annotation { "Feature Type Name" : "Feature", "Feature Type Description" : "" }
export const myFeature = defineFeature(function(context is Context, id is Id, definition is map)
    precondition{}
    {
        {
            var Q0;
            Q0=qCreatedBy(makeId("Front.planeOp"),FACE);
            var sketch = newSketch(context, id + "F0", { "sketchPlane" : qUnion([Q0])});
            skLineSegment(sketch, "E0.bottom", {"start": v(-36.81, 42.63) * mm, "end": v(35.22, 42.63) * mm});
            skLineSegment(sketch, "E0.top", {"start": v(-36.81, -38.86) * mm, "end": v(35.22, -38.86) * mm});
            skLineSegment(sketch, "E0.left", {"start": v(-36.81, 42.63) * mm, "end": v(-36.81, -38.86) * mm});
            skLineSegment(sketch, "E0.right", {"start": v(35.22, 42.63) * mm, "end": v(35.22, -38.86) * mm});
            skPoint(sketch, "E1.oppositeSnap0", {"position": v(-0.8, 42.63) * mm});
            skLineSegment(sketch, "E1.bottom", {"start": v(-26.75, 18.27) * mm, "end": v(-0.8, 18.27) * mm});
            skLineSegment(sketch, "E1.top", {"start": v(-26.75, 12.97) * mm, "end": v(-0.8, 12.97) * mm});
            skLineSegment(sketch, "E1.left", {"start": v(-26.75, 18.27) * mm, "end": v(-26.75, 12.97) * mm});
            skLineSegment(sketch, "E1.right", {"start": v(-0.8, 18.27) * mm, "end": v(-0.8, 12.97) * mm});
            skLineSegment(sketch, "E2.bottom", {"start": v(-27.28, 28.86) * mm, "end": v(-0.8, 28.86) * mm});
            skLineSegment(sketch, "E2.top", {"start": v(-27.28, 23.04) * mm, "end": v(-0.8, 23.04) * mm});
            skLineSegment(sketch, "E2.left", {"start": v(-27.28, 28.86) * mm, "end": v(-27.28, 23.04) * mm});
            skLineSegment(sketch, "E2.right", {"start": v(-0.8, 28.86) * mm, "end": v(-0.8, 23.04) * mm});
            skCircle(sketch, "E3", {"center": v(0, -19.34) * mm, "radius": 3.71 * mm});
            skLineSegment(sketch, "E4.bottom", {"start": v(0, 16.29) * mm, "end": v(5.18, 16.29) * mm});
            skLineSegment(sketch, "E4.top", {"start": v(0, 14.47) * mm, "end": v(5.18, 14.47) * mm});
            skLineSegment(sketch, "E4.left", {"start": v(0, 16.29) * mm, "end": v(0, 14.47) * mm});
            skLineSegment(sketch, "E4.right", {"start": v(5.18, 16.29) * mm, "end": v(5.18, 14.47) * mm});
            skLineSegment(sketch, "E5.bottom", {"start": v(0, 26.75) * mm, "end": v(5.18, 26.75) * mm});
            skLineSegment(sketch, "E5.top", {"start": v(0, 24.7) * mm, "end": v(5.18, 24.7) * mm});
            skLineSegment(sketch, "E5.left", {"start": v(0, 26.75) * mm, "end": v(0, 24.7) * mm});
            skLineSegment(sketch, "E5.right", {"start": v(5.18, 26.75) * mm, "end": v(5.18, 24.7) * mm});
            skLineSegment(sketch, "E6.bottom", {"start": v(22.23, 10.78) * mm, "end": v(24, 10.78) * mm});
            skLineSegment(sketch, "E6.top", {"start": v(22.23, 7.33) * mm, "end": v(24, 7.33) * mm});
            skLineSegment(sketch, "E6.left", {"start": v(22.23, 10.78) * mm, "end": v(22.23, 7.33) * mm});
            skLineSegment(sketch, "E6.right", {"start": v(24, 10.78) * mm, "end": v(24, 7.33) * mm});
            skLineSegment(sketch, "E7.bottom", {"start": v(28.56, 10.8) * mm, "end": v(30.37, 10.8) * mm});
            skLineSegment(sketch, "E7.top", {"start": v(28.56, 7.32) * mm, "end": v(30.37, 7.32) * mm});
            skLineSegment(sketch, "E7.left", {"start": v(30.37, 10.8) * mm, "end": v(30.37, 7.32) * mm});
            skLineSegment(sketch, "E7.right", {"start": v(28.56, 10.8) * mm, "end": v(28.56, 7.32) * mm});
            skText(sketch, "E8", { "text": "USB", "fontName": "OpenSans-Regular.ttf"});
            skPoint(sketch, "E8.firstSnap0", {"position": v(23.12, 10.78) * mm});
            skPoint(sketch, "E8.secondSnap0", {"position": v(29.47, 10.8) * mm});
            skText(sketch, "E9", { "text": "John Computers", "fontName": "OpenSans-Regular.ttf"});
            skLineSegment(sketch, "E10.bottom", {"start": v(-32.21, 0) * mm, "end": v(-30.06, 0) * mm});
            skLineSegment(sketch, "E10.top", {"start": v(-32.21, -38.86) * mm, "end": v(-30.06, -38.86) * mm});
            skLineSegment(sketch, "E10.left", {"start": v(-32.21, 0) * mm, "end": v(-32.21, -38.86) * mm});
            skLineSegment(sketch, "E10.right", {"start": v(-30.06, 0) * mm, "end": v(-30.06, -38.86) * mm});
            skLineSegment(sketch, "E11.bottom", {"start": v(-26.94, 0) * mm, "end": v(-24.3, 0) * mm});
            skLineSegment(sketch, "E11.top", {"start": v(-26.94, -38.86) * mm, "end": v(-24.3, -38.86) * mm});
            skLineSegment(sketch, "E11.left", {"start": v(-26.94, 0) * mm, "end": v(-26.94, -38.86) * mm});
            skLineSegment(sketch, "E11.right", {"start": v(-24.3, 0) * mm, "end": v(-24.3, -38.86) * mm});
            skLineSegment(sketch, "E12.bottom", {"start": v(-20.95, 0) * mm, "end": v(-18.3, 0) * mm});
            skLineSegment(sketch, "E12.top", {"start": v(-20.95, -38.86) * mm, "end": v(-18.3, -38.86) * mm});
            skLineSegment(sketch, "E12.left", {"start": v(-20.95, 0) * mm, "end": v(-20.95, -38.86) * mm});
            skLineSegment(sketch, "E12.right", {"start": v(-18.3, 0) * mm, "end": v(-18.3, -38.86) * mm});
            skLineSegment(sketch, "E13.bottom", {"start": v(-15.43, 0) * mm, "end": v(-13.28, 0) * mm});
            skLineSegment(sketch, "E13.top", {"start": v(-15.43, -38.86) * mm, "end": v(-13.28, -38.86) * mm});
            skLineSegment(sketch, "E13.left", {"start": v(-15.43, 0) * mm, "end": v(-15.43, -38.86) * mm});
            skLineSegment(sketch, "E13.right", {"start": v(-13.28, 0) * mm, "end": v(-13.28, -38.86) * mm});
            skLineSegment(sketch, "E14.bottom", {"start": v(-10.88, -0.13) * mm, "end": v(-8.95, -0.13) * mm});
            skLineSegment(sketch, "E14.top", {"start": v(-10.88, -38.86) * mm, "end": v(-8.95, -38.86) * mm});
            skLineSegment(sketch, "E14.left", {"start": v(-10.88, -0.13) * mm, "end": v(-10.88, -38.86) * mm});
            skLineSegment(sketch, "E14.right", {"start": v(-8.95, -0.13) * mm, "end": v(-8.95, -38.86) * mm});
            const initialGuessF0  = {"E8": [0.02312, 0.01078, 1, 0, 0.00236], "E9": [-0.038, 0.03264, 1, 0, 0.00695]};
            skSetInitialGuess(sketch, initialGuessF0);
            skSolve(sketch);
        }
        {
            var Q0;
            Q0=makeQuery(id+"F0.imprint","IMPRINT",FACE,{"disambiguationData":[TD([[makeQuery(id+"F0.imprint","IMPRINT",EDGE,{"derivedFrom":sQuery(id+"F0.wireOp",EDGE,"E0.bottom")}),-1.0]])]});
            extrude(context, id + "F1", {"entities" : qUnion([Q0]), "endBound" : BoundingType.SYMMETRIC, "depth" : 101.6 * mm, "offsetDistance" : 25.4 * mm});
        }
    });